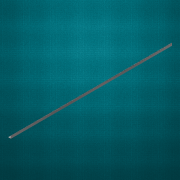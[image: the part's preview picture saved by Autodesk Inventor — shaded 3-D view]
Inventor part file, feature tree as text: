
AUTODESK INVENTOR PART (.ipt)
format: ipt  version: 2017 (Build 210142000, 142)  size: 136,192 bytes
history: native  units: in
note: dims shown in document units (in); Inventor stores cm internally (conversion verified against a paired STEP export)
features: extrude x1, sketch x1
ambient origin geometry x8: Origin, YZ Plane, XZ Plane, XY Plane, X Axis, Y Axis, Z Axis, Center Point
bodies: Solid1 (feature_tree)
feature tree (2):
  extrude  "Extrusion1"  Depth=0.0625in
  sketch  "Sketch1"  dims[d0=1.375in d1=0.0625in d2=0.0625in d4=0.125in d5=0.125in d6=1.375in d7=0.125in d8=0.0625in d9=78.875in d10=0.0in]
